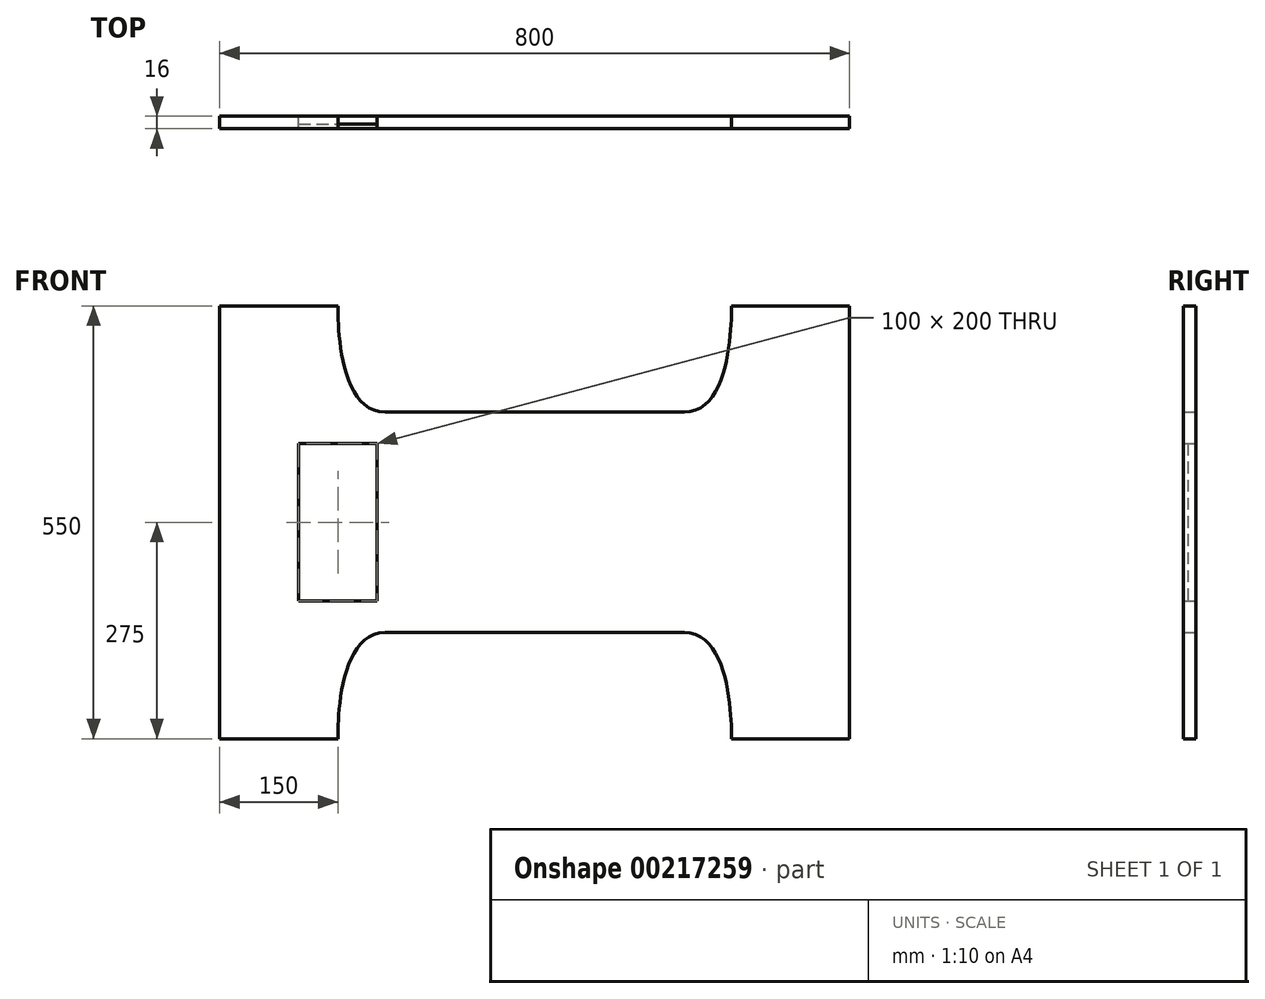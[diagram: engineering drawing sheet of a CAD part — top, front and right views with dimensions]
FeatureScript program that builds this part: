
annotation { "Feature Type Name" : "Feature", "Feature Type Description" : "" }
export const myFeature = defineFeature(function(context is Context, id is Id, definition is map)
    precondition{}
    {
        {
            var Q0;
            Q0=qCreatedBy(makeId("Front.planeOp"),FACE);
            var sketch = newSketch(context, id + "F0", { "sketchPlane" : qUnion([Q0])});
            skLineSegment(sketch, "E0.bottom", {"start": v(-400, 275) * mm, "end": v(400, 275) * mm});
            skLineSegment(sketch, "E0.top", {"start": v(-400, -275) * mm, "end": v(400, -275) * mm});
            skLineSegment(sketch, "E0.left", {"start": v(-400, 275) * mm, "end": v(-400, -275) * mm});
            skLineSegment(sketch, "E0.right", {"start": v(400, 275) * mm, "end": v(400, -275) * mm});
            skPoint(sketch, "E0.middle", {"position": v(0, 0) * mm});
            skLineSegment(sketch, "E1.bottom", {"start": v(-250, 275) * mm, "end": v(250, 275) * mm});
            skLineSegment(sketch, "E1.top", {"start": v(-250, 140) * mm, "end": v(250, 140) * mm});
            skLineSegment(sketch, "E1.left", {"start": v(-250, 275) * mm, "end": v(-250, 140) * mm});
            skLineSegment(sketch, "E1.right", {"start": v(250, 275) * mm, "end": v(250, 140) * mm});
            skFitSpline(sketch, "E2", {"points": [v(-250, 275) * mm, v(-190, 140) * mm], "startDerivative": vector(0, -55.12) * mm, "endDerivative": vector(180, 0) * mm});
            skLineSegment(sketch, "E3", {"start": v(0, 0) * mm, "end": v(0, 25.25) * mm});
            skLineSegment(sketch, "E4", {"start": v(0, 25.25) * mm, "end": v(0, 0) * mm});
            skLineSegment(sketch, "E5", {"start": v(0, 0) * mm, "end": v(-29.42, 0) * mm});
            skFitSpline(sketch, "E6.MirrorCS", {"points": [v(250, 275) * mm, v(190, 140) * mm], "startDerivative": vector(0, -55.12) * mm, "endDerivative": vector(-180, 0) * mm});
            skLineSegment(sketch, "E7.MirrorCS", {"start": v(-250, -140) * mm, "end": v(250, -140) * mm});
            skLineSegment(sketch, "E8.MirrorCS", {"start": v(-250, -275) * mm, "end": v(-250, -140) * mm});
            skFitSpline(sketch, "E9.MirrorCS", {"points": [v(-250, -275) * mm, v(-190, -140) * mm], "startDerivative": vector(0, 55.12) * mm, "endDerivative": vector(180, 0) * mm});
            skFitSpline(sketch, "E10.MirrorCS", {"points": [v(250, -275) * mm, v(190, -140) * mm], "startDerivative": vector(0, 55.12) * mm, "endDerivative": vector(-180, 0) * mm});
            skLineSegment(sketch, "E11.MirrorCS", {"start": v(250, -275) * mm, "end": v(250, -140) * mm});
            skLineSegment(sketch, "E12.bottom", {"start": v(-300, 100) * mm, "end": v(-200, 100) * mm});
            skLineSegment(sketch, "E12.top", {"start": v(-300, -100) * mm, "end": v(-200, -100) * mm});
            skLineSegment(sketch, "E12.left", {"start": v(-300, 100) * mm, "end": v(-300, -100) * mm});
            skLineSegment(sketch, "E12.right", {"start": v(-200, 100) * mm, "end": v(-200, -100) * mm});
            skSolve(sketch);
        }
        {
            var Q0;
            {var subQ7=sQuery(id+"F0.wireOp",EDGE,"E0.left");Q0=makeQuery(id+"F0.imprint","IMPRINT",FACE,{"disambiguationData":[TD([[makeQuery(id+"F0.imprint","IMPRINT",EDGE,{"derivedFrom":subQ7}),1.0]])]});}
            var Q1;
            {var subQ0=sQuery(id+"F0.wireOp",EDGE,"E1.left");Q1=makeQuery(id+"F0.imprint","IMPRINT",FACE,{"disambiguationData":[TD([[makeQuery(id+"F0.imprint","IMPRINT",EDGE,{"derivedFrom":subQ0}),1.0]])]});}
            var Q2;
            {var subQ0=sQuery(id+"F0.wireOp",EDGE,"e4a864e7-9524-4932-b981-ddb32812ea390.MirrorCS");Q2=makeQuery(id+"F0.imprint","IMPRINT",FACE,{"disambiguationData":[TD([[makeQuery(id+"F0.imprint","IMPRINT",EDGE,{"derivedFrom":subQ0}),-1.0]])]});}
            var Q3;
            {var subQ0=sQuery(id+"F0.wireOp",EDGE,"2600050a-a9bf-4127-8e1a-3d90846a541b0.MirrorCS");Q3=makeQuery(id+"F0.imprint","IMPRINT",FACE,{"disambiguationData":[TD([[makeQuery(id+"F0.imprint","IMPRINT",EDGE,{"derivedFrom":subQ0}),-1.0]])]});}
            var Q4;
            {var subQ0=sQuery(id+"F0.wireOp",EDGE,"E1.right");Q4=makeQuery(id+"F0.imprint","IMPRINT",FACE,{"disambiguationData":[TD([[makeQuery(id+"F0.imprint","IMPRINT",EDGE,{"derivedFrom":subQ0}),-1.0]])]});}
            var Q5;
            {var subQ0=sQuery(id+"F0.wireOp",EDGE,"cef0462c-00c9-4aca-9a6a-395836b52a160.MirrorCS");Q5=makeQuery(id+"F0.imprint","IMPRINT",FACE,{"disambiguationData":[TD([[makeQuery(id+"F0.imprint","IMPRINT",EDGE,{"derivedFrom":subQ0}),-1.0]])]});}
            var Q6;
            {var subQ0=sQuery(id+"F0.wireOp",EDGE,"E8.MirrorCS");Q6=makeQuery(id+"F0.imprint","IMPRINT",FACE,{"disambiguationData":[TD([[makeQuery(id+"F0.imprint","IMPRINT",EDGE,{"derivedFrom":subQ0}),-1.0]])]});}
            var Q7;
            {var subQ2=sQuery(id+"F0.wireOp",EDGE,"E10.MirrorCS");Q7=makeQuery(id+"F0.imprint","IMPRINT",FACE,{"disambiguationData":[TD([[makeQuery(id+"F0.imprint","IMPRINT",EDGE,{"derivedFrom":subQ2}),-1.0]])]});}
            extrude(context, id + "F1", {"entities" : qUnion([Q0, Q1, Q2, Q3, Q4, Q5, Q6, Q7]), "depth" : 16 * mm});
        }
        {
            var Q0;
            Q0=makeQuery(id+"F0.imprint","IMPRINT",FACE,{"disambiguationData":[TD([[makeQuery(id+"F0.imprint","IMPRINT",EDGE,{"derivedFrom":sQuery(id+"F0.wireOp",EDGE,"E12.bottom")}),-1.0]])]});
            extrude(context, id + "F2", {"entities" : qUnion([Q0]), "depth" : 10 * mm});
        }
    });
